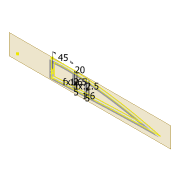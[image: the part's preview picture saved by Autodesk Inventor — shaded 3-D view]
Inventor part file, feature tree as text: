
AUTODESK INVENTOR PART (.ipt)
format: ipt  version: 2022 (Build 260153000, 153)  size: 325,120 bytes
history: native  units: mm
features: extrude x6, sketch x6, projected_geometry x4, shell x1, fillet x1, plane x1
ambient origin geometry x8: Origin, YZ Plane, XZ Plane, XY Plane, X Axis, Y Axis, Z Axis, Center Point
bodies: Solid1 (feature_tree)
feature tree (19):
  extrude  "Extrusion1"  Depth=5.0mm
  shell  "Shell1"  Thickness=6.0mm
  extrude  "Extrusion2"  Depth=2.0mm
  extrude  "Extrusion3"  Depth=5.9mm
  extrude  "Extrusion4"  Depth=10.0mm TaperAngle=0.0deg
  fillet  "Fillet1"  Radius=70.0mm
  plane  "Work Plane1"
  extrude  "Extrusion5"  Depth=4.0mm TaperAngle=0.0deg
  extrude  "Extrusion8"  Depth=0.5mm
  sketch  "Sketch3"  dims[d0=4.0mm d1=0.0mm d2=5.0mm d3=6.0mm]
  sketch  "Sketch7"  dims[d5=4.0mm d6=0.0mm d7=2.0mm]
  projected_geometry  "Projected Loop3"
  sketch  "Sketch8"  dims[d8=2.0mm d9=5.9mm]
  sketch  "Sketch9"  dims[d12=5.0mm d13=10.0mm d14=0.0mm d15=70.0mm]
  sketch  "Sketch10"  dims[d16=10.0mm d17=0.0mm d22=4.0mm d23=0.0mm]
  projected_geometry  "Projected Loop4"
  projected_geometry  "Projected Loop10"
  sketch  "Sketch16"  dims[d24=2.0mm d26=2.0mm d31=2.0mm d32=5.0mm d34=1.6mm d35=2.5mm d37=5.0mm d38=1.6mm d40=2.5mm d41=45.0mm d42=20.0mm d43=0.5mm d44=10.0mm d45=0.0mm]
  projected_geometry  "Projected Loop11"
